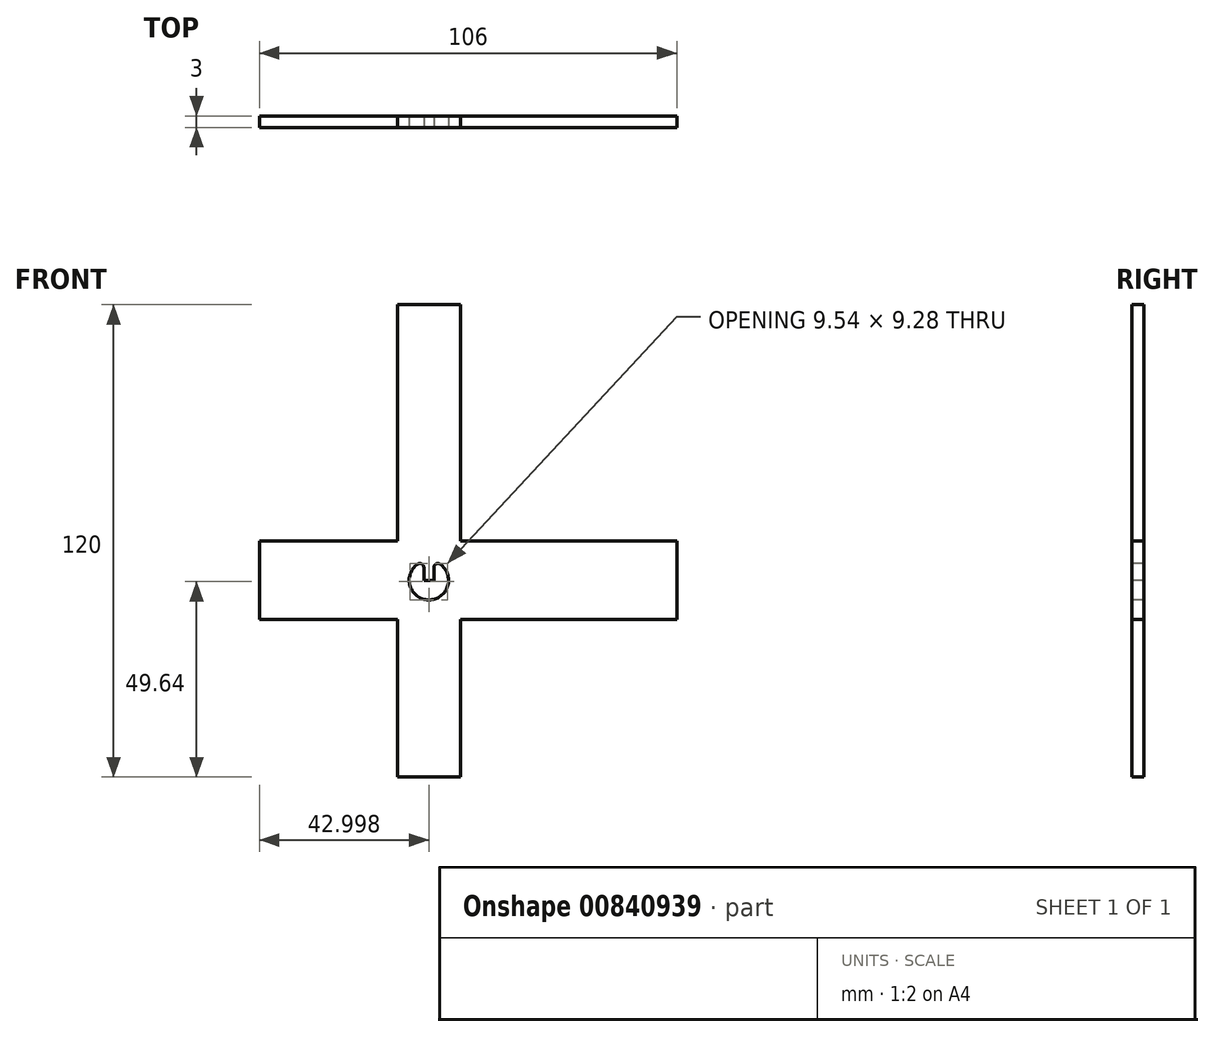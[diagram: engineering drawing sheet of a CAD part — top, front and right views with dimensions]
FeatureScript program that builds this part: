
annotation { "Feature Type Name" : "Feature", "Feature Type Description" : "" }
export const myFeature = defineFeature(function(context is Context, id is Id, definition is map)
    precondition{}
    {
        {
            var Q0;
            Q0=qCreatedBy(makeId("Front.planeOp"),FACE);
            var sketch = newSketch(context, id + "F0", { "sketchPlane" : qUnion([Q0])});
            skLineSegment(sketch, "E0", {"start": v(-10.92, -44.72) * mm, "end": v(-10.92, -4.72) * mm});
            skLineSegment(sketch, "E1", {"start": v(-10.92, -4.72) * mm, "end": v(-45.92, -4.72) * mm});
            skLineSegment(sketch, "E2", {"start": v(-45.92, -4.72) * mm, "end": v(-45.92, 15.28) * mm});
            skLineSegment(sketch, "E3", {"start": v(-45.92, 15.28) * mm, "end": v(-10.92, 15.28) * mm});
            skLineSegment(sketch, "E4", {"start": v(-10.92, 15.28) * mm, "end": v(-10.92, 75.28) * mm});
            skLineSegment(sketch, "E5", {"start": v(-10.92, 75.28) * mm, "end": v(5.08, 75.28) * mm});
            skLineSegment(sketch, "E6", {"start": v(5.08, 75.28) * mm, "end": v(5.08, 15.28) * mm});
            skLineSegment(sketch, "E7", {"start": v(5.08, 15.28) * mm, "end": v(60.08, 15.28) * mm});
            skLineSegment(sketch, "E8", {"start": v(60.08, 15.28) * mm, "end": v(60.08, -4.72) * mm});
            skLineSegment(sketch, "E9", {"start": v(60.08, -4.72) * mm, "end": v(5.08, -4.72) * mm});
            skLineSegment(sketch, "E10", {"start": v(5.08, -4.72) * mm, "end": v(5.08, -44.72) * mm});
            skLineSegment(sketch, "E11", {"start": v(5.08, -44.72) * mm, "end": v(-10.92, -44.72) * mm});
            skSolve(sketch);
        }
        {
            var Q0;
            Q0 = qSketchRegion(id + "F0", true);
            extrude(context, id + "F1", {"entities" : qUnion([Q0]), "depth" : 3 * mm, "offsetDistance" : 25 * mm});
        }
        {
            var Q0;
            Q0=makeQuery(id+"F1.opExtrude","CAP_FACE",FACE,{"disambiguationData":[OSD([sQuery(id+"F0.wireOp",EDGE,"E0"),sQuery(id+"F0.wireOp",EDGE,"E1"),sQuery(id+"F0.wireOp",EDGE,"E2"),sQuery(id+"F0.wireOp",EDGE,"E3"),sQuery(id+"F0.wireOp",EDGE,"E4"),sQuery(id+"F0.wireOp",EDGE,"E5"),sQuery(id+"F0.wireOp",EDGE,"E6"),sQuery(id+"F0.wireOp",EDGE,"E7"),sQuery(id+"F0.wireOp",EDGE,"E8"),sQuery(id+"F0.wireOp",EDGE,"E9"),sQuery(id+"F0.wireOp",EDGE,"E10"),sQuery(id+"F0.wireOp",EDGE,"E11")])],"isStart":false});
            var sketch = newSketch(context, id + "F2", { "sketchPlane" : qUnion([Q0])});
            skArc(sketch, "E12", {"start": v(-5.78, 9.38) * mm, "mid": v(-2.92, 0.28) * mm, "end": v(-0.06, 9.38) * mm});
            skPoint(sketch, "E12.centerSnap0", {"position": v(-2.92, 75.28) * mm});
            skPoint(sketch, "E12.centerSnap1", {"position": v(60.08, 5.28) * mm});
            skLineSegment(sketch, "E13.top", {"start": v(-4.2, 5.28) * mm, "end": v(-1.64, 5.28) * mm});
            skLineSegment(sketch, "E13.left", {"start": v(-4.2, 8.56) * mm, "end": v(-4.2, 5.28) * mm});
            skLineSegment(sketch, "E13.right", {"start": v(-1.64, 8.56) * mm, "end": v(-1.64, 5.28) * mm});
            skPoint(sketch, "E14.visualSharp", {"position": v(-4.2, 10.11) * mm});
            skArc(sketch, "E14.filletArc", {"start": v(-4.2, 8.56) * mm, "mid": v(-4.75, 9.45) * mm, "end": v(-5.78, 9.38) * mm});
            skPoint(sketch, "E15.visualSharp", {"position": v(-1.64, 10.11) * mm});
            skArc(sketch, "E15.filletArc", {"start": v(-0.06, 9.38) * mm, "mid": v(-1.1, 9.45) * mm, "end": v(-1.64, 8.56) * mm});
            skSolve(sketch);
        }
        {
            var Q0;
            Q0 = qSketchRegion(id + "F2", true);
            extrude(context, id + "F3", {"entities" : qUnion([Q0]), "operationType" : NewBodyOperationType.REMOVE, "oppositeDirection" : true, "depth" : 25 * mm, "offsetDistance" : 25 * mm});
        }
    });
